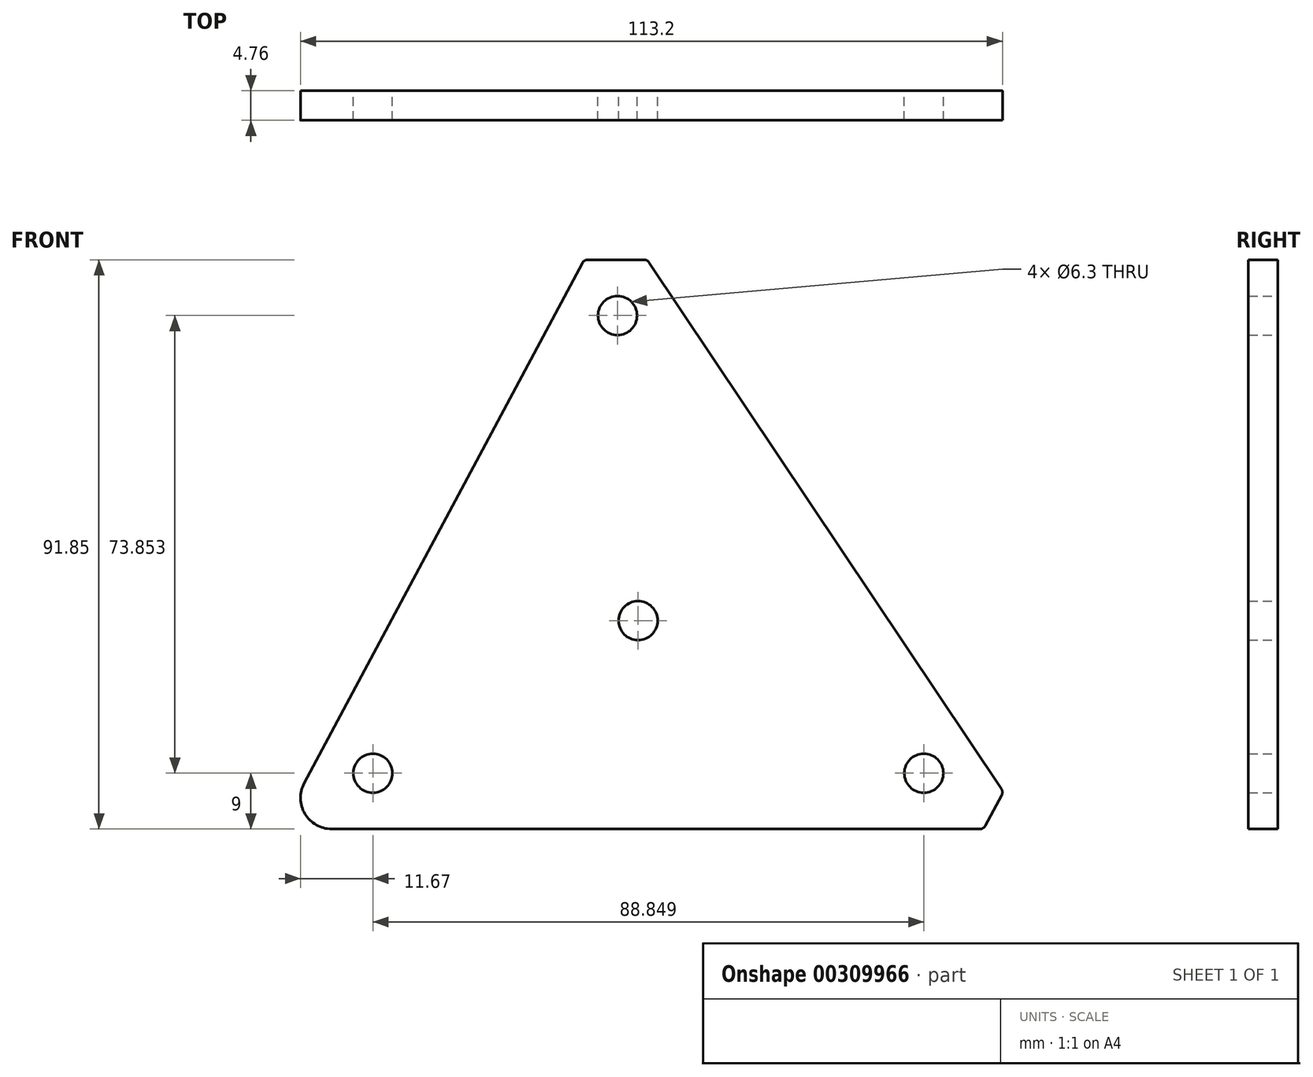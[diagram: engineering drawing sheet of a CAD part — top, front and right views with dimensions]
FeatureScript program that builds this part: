
annotation { "Feature Type Name" : "Feature", "Feature Type Description" : "" }
export const myFeature = defineFeature(function(context is Context, id is Id, definition is map)
    precondition{}
    {
        {
            var Q0;
            Q0=qCreatedBy(makeId("Front.planeOp"),FACE);
            var sketch = newSketch(context, id + "F0", { "sketchPlane" : qUnion([Q0])});
            skLineSegment(sketch, "E0", {"start": v(0, 0) * mm, "end": v(39.45, 73.85) * mm, "construction": true});
            skLineSegment(sketch, "E1", {"start": v(39.45, 73.85) * mm, "end": v(88.85, 0) * mm, "construction": true});
            skLineSegment(sketch, "E2", {"start": v(88.85, 0) * mm, "end": v(0, 0) * mm, "construction": true});
            skPoint(sketch, "E3", {"position": v(42.77, 24.62) * mm});
            skLineSegment(sketch, "E4.0", {"start": v(97.9, -9) * mm, "end": v(-6.67, -9) * mm});
            skLineSegment(sketch, "E5.0", {"start": v(44.56, 82.4) * mm, "end": v(101.36, -2.51) * mm});
            skCircle(sketch, "E6", {"center": v(39.45, 73.85) * mm, "radius": 3.15 * mm});
            skCircle(sketch, "E7", {"center": v(0, 0) * mm, "radius": 3.15 * mm});
            skCircle(sketch, "E8", {"center": v(88.85, 0) * mm, "radius": 3.15 * mm});
            skCircle(sketch, "E9", {"center": v(42.77, 24.62) * mm, "radius": 3.15 * mm});
            skLineSegment(sketch, "E10.0", {"start": v(-11.08, -1.64) * mm, "end": v(33.78, 82.32) * mm});
            skLineSegment(sketch, "E11", {"start": v(34.66, 82.85) * mm, "end": v(43.73, 82.85) * mm});
            skArc(sketch, "E12.filletArc", {"start": v(-11.08, -1.64) * mm, "mid": v(-10.96, -6.57) * mm, "end": v(-6.67, -9) * mm});
            skLineSegment(sketch, "E13", {"start": v(101.4, -3.54) * mm, "end": v(98.77, -8.47) * mm});
            skPoint(sketch, "E14.visualSharp", {"position": v(98.49, -9) * mm});
            skArc(sketch, "E14.filletArc", {"start": v(97.9, -9) * mm, "mid": v(98.4, -8.86) * mm, "end": v(98.77, -8.47) * mm});
            skPoint(sketch, "E15.visualSharp", {"position": v(101.69, -3.01) * mm});
            skArc(sketch, "E15.filletArc", {"start": v(101.4, -3.54) * mm, "mid": v(101.52, -3.02) * mm, "end": v(101.36, -2.51) * mm});
            skPoint(sketch, "E16.visualSharp", {"position": v(34.06, 82.85) * mm});
            skArc(sketch, "E16.filletArc", {"start": v(34.66, 82.85) * mm, "mid": v(34.14, 82.71) * mm, "end": v(33.78, 82.32) * mm});
            skPoint(sketch, "E17.visualSharp", {"position": v(44.26, 82.85) * mm});
            skArc(sketch, "E17.filletArc", {"start": v(44.56, 82.4) * mm, "mid": v(44.2, 82.74) * mm, "end": v(43.73, 82.85) * mm});
            skSolve(sketch);
        }
        {
            var Q0;
            Q0 = qSketchRegion(id + "F0", true);
            extrude(context, id + "F1", {"entities" : qUnion([Q0]), "depth" : 4.76 * mm});
        }
    });
